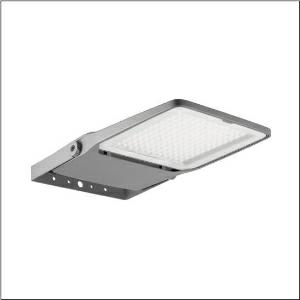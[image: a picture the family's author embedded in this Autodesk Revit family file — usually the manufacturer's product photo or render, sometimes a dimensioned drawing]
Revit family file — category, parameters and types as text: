
# Revit family: floodlight_fl_20_midi___rs17_5xa7682e3b2ac_f562
name_source: partatom
category: Lighting Fixtures
units: mm (PartAtom-declared; Revit-internal decimal feet)

## family parameters
Cut with Voids When Loaded = No
Host = Face
Light Source = No
Part Type = Normal
Room Calculation Point = No
Round Connector Dimension = Use Diameter
Shared = No

## types (1)
- --- (1 x LED 5000K / CRI = 70 (unbekannt), 29600 lm, 5000K)
    Apparent Load = 208 VA
    CIE Flux Codes = 79 92 99 100 100
    Color Rendering = 70
    Color Temperature = 5000K
    Default Elevation = 1800 mm
    Description = Floodlight FL 20 midi, floodlight, primary light control with lens, of plastic, primary optical cover: protective disc, of toughened safety glass, transparent, light distribution: RS17, light emission: direct distribution, primary light characteristic: rotationally symmetric, installation type: surface-mounted, LED High Power LED, rated luminous flux: 29.600 lm, light colour: 750, colour temperature: 5000K, control gear: ECG Plus, control: flexible luminous flux parameterisation, time-dependent luminous flux control, digital communication interface, power reduction, overheat protection, electronic power reduction, with terminal, 5-pole, max. 2.5mm², mains connection: 220..240V, AC, 50/60Hz, rated input power: 208W, LED unit, of diecast aluminium, powder-coated, Siteco® metallic grey (DB 702S), length: 731 mm, width: 450 mm, height: 76mm, housing frame, of diecast aluminium, powder-coated, Siteco® metallic grey (DB 702S), wall fastening, of steel, powder-coated, Siteco® metallic grey (DB 702S), DALIprotection rating (complete): IP66, insulation class (complete): insulation class II (safety insulation), certification: CE, ENEC, VDE, protection symbol: D, permissible ambient temperature for indoor applications: -40..+40°C, permissible ambient temperature for outdoor applications: -40..+50°C, standard: DIN EN 12944, packaging unit: 1 piece

Light Distribution: RS17
    Height = 76 mm
    Lamp = 1 x LED 5000K / CRI >= 70 (unbekannt)
    Lamp Light Flux = 29600 lm
    Lamp count = 1
    Length = 731 mm
    Luminous efficacy = 142 lm/W
    Manufacturer = Siteco
    ModVariant = No
    Model = 5XA7682E3B2AC
    Number of Poles = 1
    OnlyDefault = Yes
    Power Factor = 1
    Product Name = Floodlight FL 20 midi | RS17
    Product group = floodlight | pylon top
    ProductGroupID = 6101
    Protection Class = Protection class II
    Protection Degree = IP 66
    RLX_Detail_Level = 1
    RlxData = <blob elided: 86369 chars, md5=9bcd8704>
    Socket = socket
    Standby Power = 0 W
    System Light Flux = 29600 lm
    System Power = 208 W
    Type Comments = factory setting: luminous flux: 100 % | dim-lin: 254 | 484 mA
    Type Image = l_1005944.jpg
    URL = http://relux.com
    VarID = @adj_141705
    Voltage = 0 V
    Weight = 0.00 kg
    Width = 450 mm

## geometry (parser evidence)
native form markers: Blend x4, Sweep x13
no freeform markers — native parametric forms only
